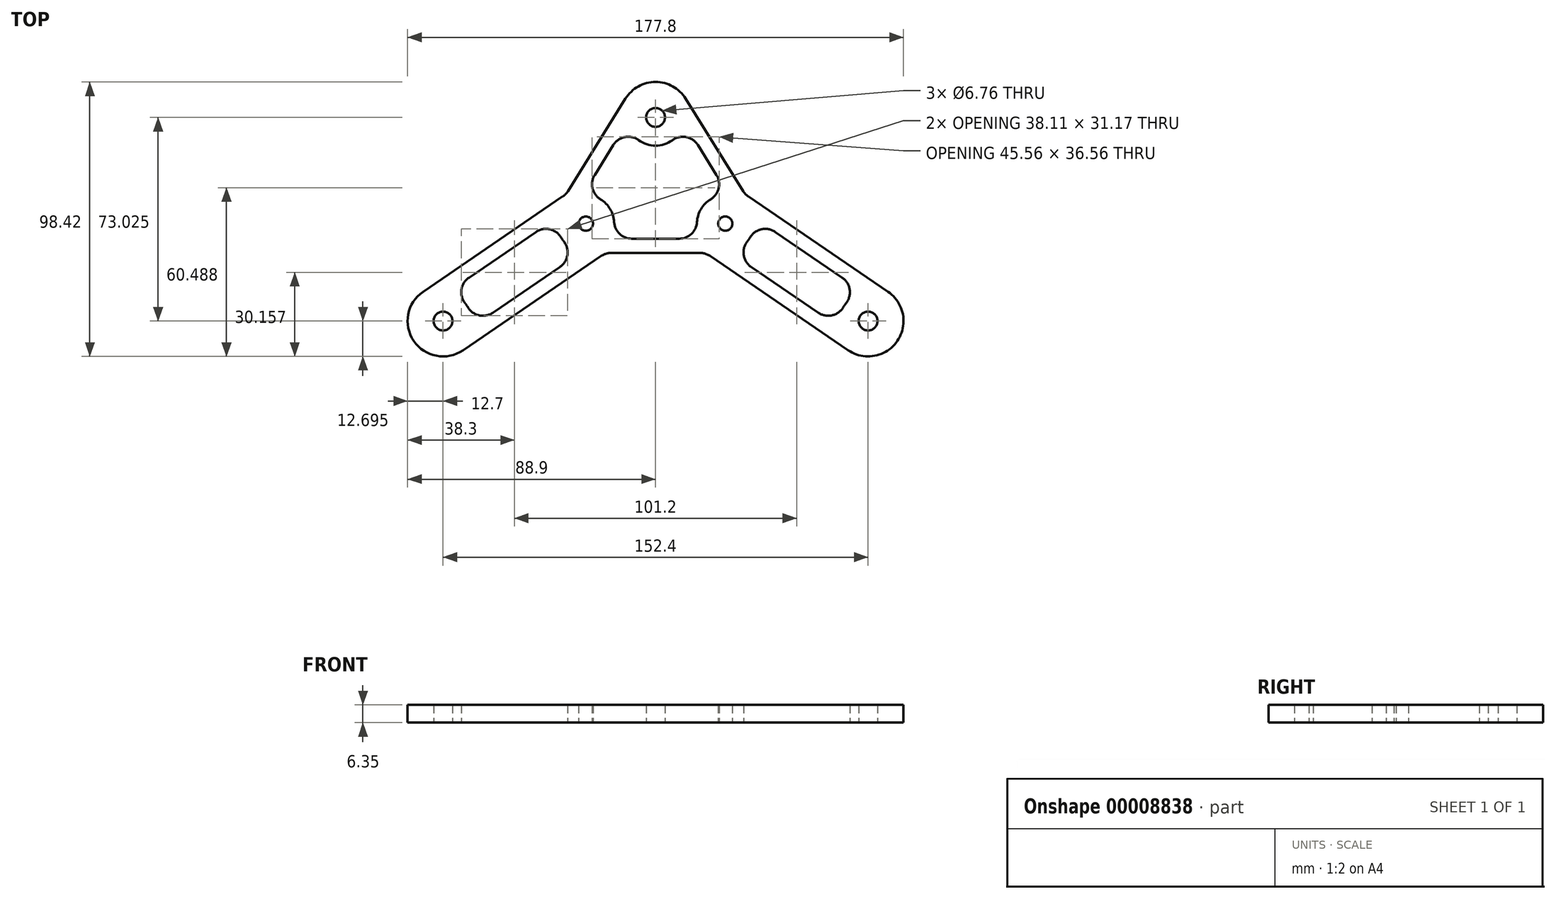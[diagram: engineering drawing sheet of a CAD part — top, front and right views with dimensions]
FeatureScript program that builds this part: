
annotation { "Feature Type Name" : "Feature", "Feature Type Description" : "" }
export const myFeature = defineFeature(function(context is Context, id is Id, definition is map)
    precondition{}
    {
        {
            var Q0;
            Q0=qCreatedBy(makeId("Top.planeOp"),FACE);
            var sketch = newSketch(context, id + "F0", { "sketchPlane" : qUnion([Q0])});
            skCircle(sketch, "E0", {"center": v(-25, 0) * mm, "radius": 2.55 * mm});
            skCircle(sketch, "E1.0.MirrorC", {"center": v(25, 0) * mm, "radius": 2.55 * mm});
            skCircle(sketch, "E2", {"center": v(-76.2, -34.93) * mm, "radius": 3.38 * mm});
            skCircle(sketch, "E3", {"center": v(0, 38.1) * mm, "radius": 3.38 * mm});
            skCircle(sketch, "E4.0.MirrorC", {"center": v(76.2, -34.93) * mm, "radius": 3.38 * mm});
            skSolve(sketch);
        }
        {
            var Q0;
            Q0=qCreatedBy(makeId("Top.planeOp"),FACE);
            var sketch = newSketch(context, id + "F1", { "sketchPlane" : qUnion([Q0])});
            skArc(sketch, "E5", {"start": v(-83.36, -24.43) * mm, "mid": v(-86.7, -42.08) * mm, "end": v(-69.04, -45.42) * mm});
            skCircle(sketch, "E6", {"center": v(-25, 0) * mm, "radius": 12.7 * mm, "construction": true});
            skArc(sketch, "E7", {"start": v(10.78, 44.81) * mm, "mid": v(0, 50.8) * mm, "end": v(-10.78, 44.81) * mm});
            skLineSegment(sketch, "E8", {"start": v(-83.36, -24.43) * mm, "end": v(-33.26, 9.74) * mm});
            skLineSegment(sketch, "E9", {"start": v(-10.78, 44.81) * mm, "end": v(-31.45, 11.63) * mm});
            skLineSegment(sketch, "E10", {"start": v(-69.04, -45.42) * mm, "end": v(-19.46, -11.6) * mm});
            skLineSegment(sketch, "E11", {"start": v(-32.16, 10.5) * mm, "end": v(-17.84, -10.5) * mm, "construction": true});
            skPoint(sketch, "E12.visualSharp", {"position": v(-32.16, 10.5) * mm});
            skArc(sketch, "E12.filletArc", {"start": v(-33.26, 9.74) * mm, "mid": v(-32.26, 10.59) * mm, "end": v(-31.45, 11.63) * mm});
            skLineSegment(sketch, "E13.0.MirrorCS", {"start": v(10.78, 44.81) * mm, "end": v(31.45, 11.63) * mm});
            skLineSegment(sketch, "E14.0.MirrorCS", {"start": v(83.36, -24.43) * mm, "end": v(33.26, 9.74) * mm});
            skArc(sketch, "E15.0.MirrorC", {"start": v(83.36, -24.43) * mm, "mid": v(86.7, -42.08) * mm, "end": v(69.04, -45.42) * mm});
            skLineSegment(sketch, "E16.0.MirrorCS", {"start": v(69.04, -45.42) * mm, "end": v(19.46, -11.6) * mm});
            skCircle(sketch, "E17.0.MirrorC", {"center": v(25, 0) * mm, "radius": 12.7 * mm, "construction": true});
            skLineSegment(sketch, "E18", {"start": v(-15.88, -10.5) * mm, "end": v(15.88, -10.5) * mm});
            skPoint(sketch, "E19.visualSharp", {"position": v(-17.84, -10.5) * mm});
            skArc(sketch, "E19.filletArc", {"start": v(-15.88, -10.5) * mm, "mid": v(-17.76, -10.77) * mm, "end": v(-19.46, -11.6) * mm});
            skPoint(sketch, "E20.visualSharp", {"position": v(17.84, -10.5) * mm});
            skArc(sketch, "E20.filletArc", {"start": v(19.46, -11.6) * mm, "mid": v(17.76, -10.77) * mm, "end": v(15.88, -10.5) * mm});
            skArc(sketch, "E21.0.MirrorCS", {"start": v(33.26, 9.74) * mm, "mid": v(32.26, 10.59) * mm, "end": v(31.45, 11.63) * mm});
            skSolve(sketch);
        }
        {
            var Q0;
            Q0=qCreatedBy(makeId("Top.planeOp"),FACE);
            var sketch = newSketch(context, id + "F2", { "sketchPlane" : qUnion([Q0])});
            skArc(sketch, "E22", {"start": v(-67.4, -29.86) * mm, "mid": v(-67.8, -29.2) * mm, "end": v(-68.27, -28.57) * mm});
            skArc(sketch, "E23", {"start": v(-33.8, -5.06) * mm, "mid": v(-33.4, -5.73) * mm, "end": v(-32.93, -6.35) * mm});
            skArc(sketch, "E24", {"start": v(-6.02, 29.91) * mm, "mid": v(0, 27.94) * mm, "end": v(6.02, 29.91) * mm});
            skLineSegment(sketch, "E25", {"start": v(-66.9, -19.35) * mm, "end": v(-42.9, -2.98) * mm});
            skLineSegment(sketch, "E26", {"start": v(-58.3, -31.94) * mm, "end": v(-34.3, -15.57) * mm});
            skLineSegment(sketch, "E27", {"start": v(-15.17, 28.16) * mm, "end": v(-21.82, 17.47) * mm});
            skArc(sketch, "E28.0.MirrorC", {"start": v(14.86, 0.58) * mm, "mid": v(16.3, 5.23) * mm, "end": v(19.73, 8.69) * mm});
            skLineSegment(sketch, "E29", {"start": v(-8.52, -5.41) * mm, "end": v(8.52, -5.41) * mm});
            skLineSegment(sketch, "E30.0.MirrorCS", {"start": v(15.17, 28.16) * mm, "end": v(21.82, 17.47) * mm});
            skArc(sketch, "E31.trimOffspring", {"start": v(-14.86, 0.58) * mm, "mid": v(-16.3, 5.23) * mm, "end": v(-19.73, 8.69) * mm});
            skPoint(sketch, "E32.visualSharp", {"position": v(-74.94, -24.84) * mm});
            skArc(sketch, "E32.filletArc", {"start": v(-66.9, -19.35) * mm, "mid": v(-69.6, -23.66) * mm, "end": v(-68.27, -28.57) * mm});
            skPoint(sketch, "E33.visualSharp", {"position": v(-66.35, -37.43) * mm});
            skArc(sketch, "E33.filletArc", {"start": v(-67.4, -29.86) * mm, "mid": v(-63.3, -32.89) * mm, "end": v(-58.3, -31.94) * mm});
            skPoint(sketch, "E34.visualSharp", {"position": v(-26.26, -10.08) * mm});
            skArc(sketch, "E34.filletArc", {"start": v(-34.3, -15.57) * mm, "mid": v(-31.6, -11.26) * mm, "end": v(-32.93, -6.35) * mm});
            skPoint(sketch, "E35.visualSharp", {"position": v(-34.85, 2.5) * mm});
            skArc(sketch, "E35.filletArc", {"start": v(-33.8, -5.06) * mm, "mid": v(-37.9, -2.04) * mm, "end": v(-42.9, -2.98) * mm});
            skPoint(sketch, "E36.visualSharp", {"position": v(-26.44, 10.06) * mm});
            skArc(sketch, "E36.filletArc", {"start": v(-21.82, 17.47) * mm, "mid": v(-22.61, 12.64) * mm, "end": v(-19.73, 8.69) * mm});
            skPoint(sketch, "E37.visualSharp", {"position": v(-16.4, -5.41) * mm});
            skArc(sketch, "E37.filletArc", {"start": v(-14.86, 0.58) * mm, "mid": v(-12.88, -3.68) * mm, "end": v(-8.52, -5.41) * mm});
            skPoint(sketch, "E38.visualSharp", {"position": v(16.4, -5.41) * mm});
            skArc(sketch, "E38.filletArc", {"start": v(8.52, -5.41) * mm, "mid": v(12.88, -3.68) * mm, "end": v(14.86, 0.58) * mm});
            skPoint(sketch, "E39.visualSharp", {"position": v(26.44, 10.06) * mm});
            skArc(sketch, "E39.filletArc", {"start": v(19.73, 8.69) * mm, "mid": v(22.61, 12.64) * mm, "end": v(21.82, 17.47) * mm});
            skPoint(sketch, "E40.visualSharp", {"position": v(10.02, 36.42) * mm});
            skArc(sketch, "E40.filletArc", {"start": v(15.17, 28.16) * mm, "mid": v(10.98, 31.03) * mm, "end": v(6.02, 29.91) * mm});
            skPoint(sketch, "E41.visualSharp", {"position": v(-10.02, 36.42) * mm});
            skArc(sketch, "E41.filletArc", {"start": v(-6.02, 29.91) * mm, "mid": v(-10.98, 31.03) * mm, "end": v(-15.17, 28.16) * mm});
            skArc(sketch, "E42.0.MirrorCS", {"start": v(34.3, -15.57) * mm, "mid": v(31.6, -11.26) * mm, "end": v(32.93, -6.35) * mm});
            skArc(sketch, "E43.0.MirrorCS", {"start": v(33.8, -5.06) * mm, "mid": v(37.9, -2.04) * mm, "end": v(42.9, -2.98) * mm});
            skArc(sketch, "E44.0.MirrorCS", {"start": v(66.9, -19.35) * mm, "mid": v(69.6, -23.66) * mm, "end": v(68.27, -28.57) * mm});
            skArc(sketch, "E45.0.MirrorCS", {"start": v(67.4, -29.86) * mm, "mid": v(63.3, -32.89) * mm, "end": v(58.3, -31.94) * mm});
            skLineSegment(sketch, "E46.0.MirrorCS", {"start": v(58.3, -31.94) * mm, "end": v(34.3, -15.57) * mm});
            skLineSegment(sketch, "E47.0.MirrorCS", {"start": v(66.9, -19.35) * mm, "end": v(42.9, -2.98) * mm});
            skArc(sketch, "E48.0.MirrorCS", {"start": v(33.8, -5.06) * mm, "mid": v(33.4, -5.73) * mm, "end": v(32.93, -6.35) * mm});
            skArc(sketch, "E49.0.MirrorCS", {"start": v(67.4, -29.86) * mm, "mid": v(67.8, -29.2) * mm, "end": v(68.27, -28.57) * mm});
            skSolve(sketch);
        }
        {
            var Q0;
            Q0=makeQuery(id+"F1.imprint","IMPRINT",FACE,{"disambiguationData":[TD([[makeQuery(id+"F1.imprint","IMPRINT",EDGE,{"derivedFrom":sQuery(id+"F1.wireOp",EDGE,"E5")}),1.0]])]});
            extrude(context, id + "F3", {"entities" : qUnion([Q0]), "depth" : 6.35 * mm});
        }
        {
            var Q0;
            Q0 = qSketchRegion(id + "F0", true);
            var Q1;
            Q1 = qSketchRegion(id + "F2", true);
            extrude(context, id + "F4", {"entities" : qUnion([Q0, Q1]), "operationType" : NewBodyOperationType.REMOVE, "endBound" : BoundingType.THROUGH_ALL, "depth" : 25.4 * mm});
        }
    });
